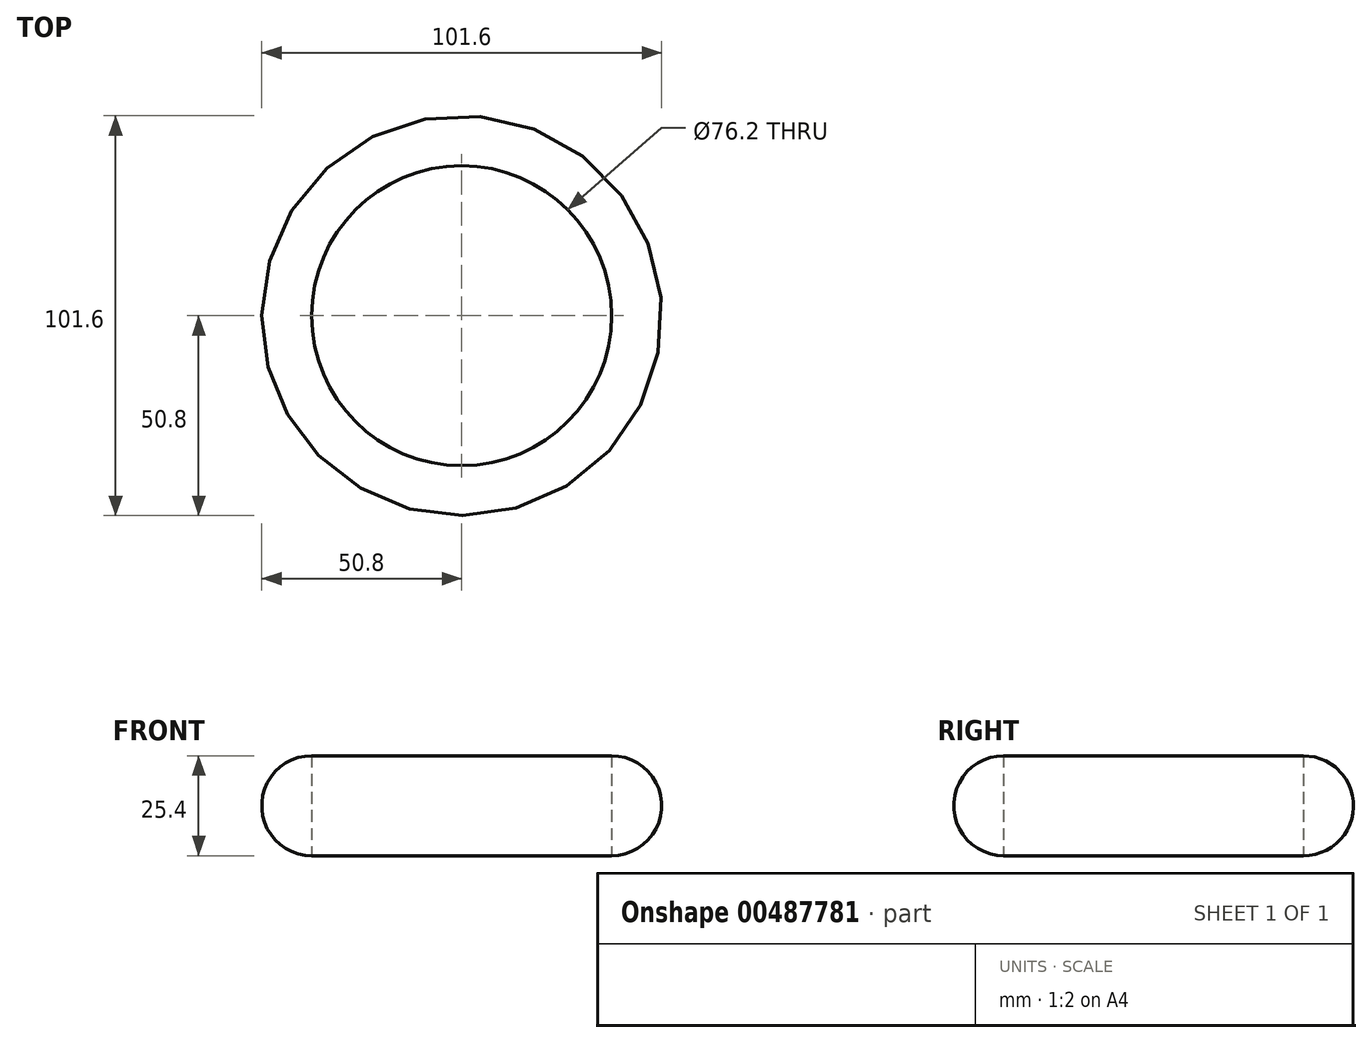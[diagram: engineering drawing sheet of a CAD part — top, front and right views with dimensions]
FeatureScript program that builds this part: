
annotation { "Feature Type Name" : "Feature", "Feature Type Description" : "" }
export const myFeature = defineFeature(function(context is Context, id is Id, definition is map)
    precondition{}
    {
        {
            var Q0;
            Q0=qCreatedBy(makeId("Front.planeOp"),FACE);
            var sketch = newSketch(context, id + "F0", { "sketchPlane" : qUnion([Q0])});
            skArc(sketch, "E0", {"start": v(38.1, -12.7) * mm, "mid": v(50.8, 0) * mm, "end": v(38.1, 12.7) * mm});
            skLineSegment(sketch, "E1", {"start": v(38.1, 12.7) * mm, "end": v(38.1, -12.7) * mm});
            skLineSegment(sketch, "E2", {"start": v(0, 0) * mm, "end": v(0, 44.82) * mm, "construction": true});
            skSolve(sketch);
        }
        {
            var Q0;
            Q0=makeQuery(id+"F0.imprint","IMPRINT",FACE,{"disambiguationData":[TD([[makeQuery(id+"F0.imprint","IMPRINT",EDGE,{"derivedFrom":sQuery(id+"F0.wireOp",EDGE,"E0")}),1.0]])]});
            var Q1;
            Q1=sQuery(id+"F0.wireOp",EDGE,"E2");
            revolve(context, id + "F1", {"entities" : qUnion([Q0]), "axis" : qUnion([Q1]), "revolveType" : RevolveType.FULL});
        }
    });
